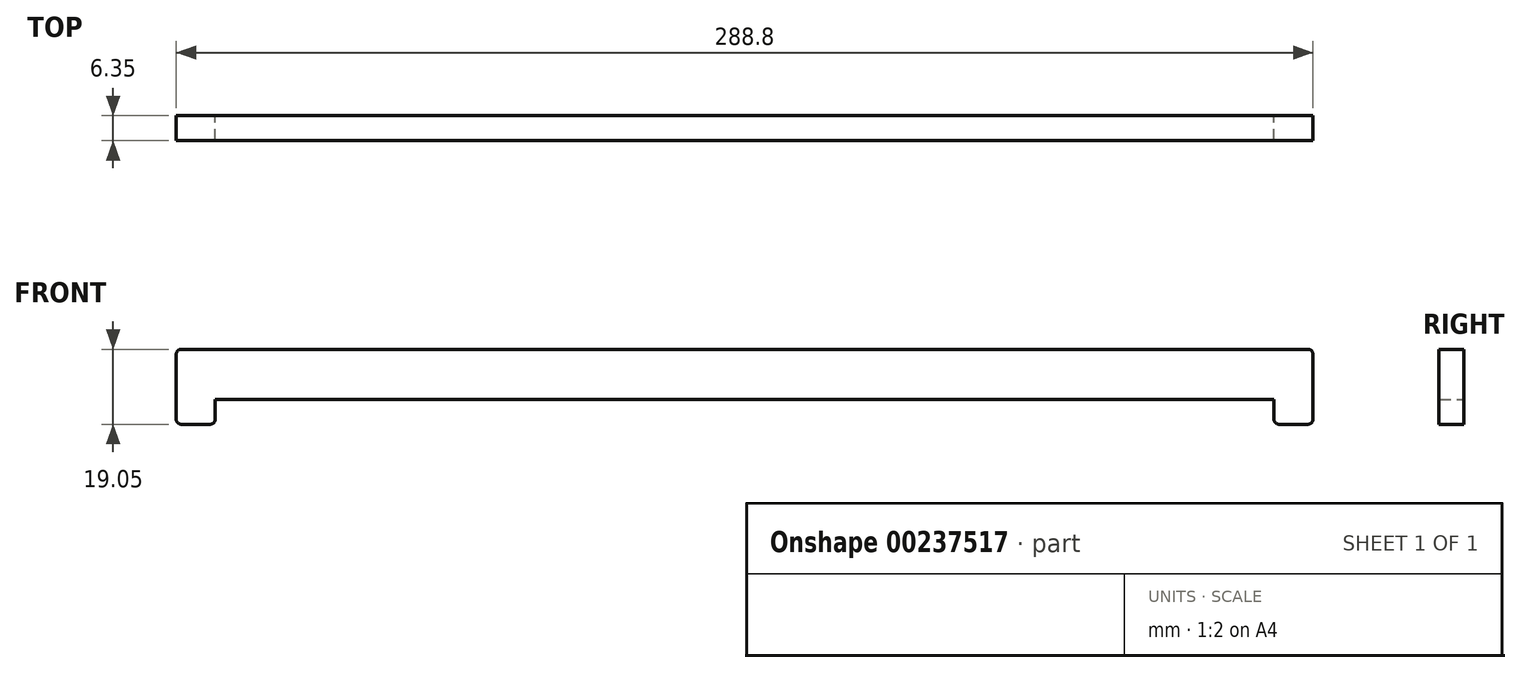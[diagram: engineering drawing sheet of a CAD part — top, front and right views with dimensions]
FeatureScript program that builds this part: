
annotation { "Feature Type Name" : "Feature", "Feature Type Description" : "" }
export const myFeature = defineFeature(function(context is Context, id is Id, definition is map)
    precondition{}
    {
        {
            var Q0;
            Q0=qCreatedBy(makeId("Front.planeOp"),FACE);
            var sketch = newSketch(context, id + "F0", { "sketchPlane" : qUnion([Q0])});
            skLineSegment(sketch, "E0", {"start": v(0, 1.27) * mm, "end": v(0, 17.78) * mm});
            skLineSegment(sketch, "E1", {"start": v(1.27, 19.05) * mm, "end": v(287.53, 19.05) * mm});
            skLineSegment(sketch, "E2", {"start": v(288.8, 17.78) * mm, "end": v(288.8, 1.27) * mm});
            skLineSegment(sketch, "E3", {"start": v(287.53, 0) * mm, "end": v(280.16, 0) * mm});
            skLineSegment(sketch, "E4", {"start": v(278.9, 1.27) * mm, "end": v(278.9, 6.35) * mm});
            skLineSegment(sketch, "E5", {"start": v(278.9, 6.35) * mm, "end": v(9.9, 6.35) * mm});
            skLineSegment(sketch, "E6", {"start": v(9.9, 6.35) * mm, "end": v(9.9, 1.27) * mm});
            skLineSegment(sketch, "E7", {"start": v(8.64, 0) * mm, "end": v(1.27, 0) * mm});
            skPoint(sketch, "E8.visualSharp", {"position": v(0, 19.05) * mm});
            skArc(sketch, "E8.filletArc", {"start": v(1.27, 19.05) * mm, "mid": v(0.37, 18.68) * mm, "end": v(0, 17.78) * mm});
            skPoint(sketch, "E9.visualSharp", {"position": v(0, 0) * mm});
            skArc(sketch, "E9.filletArc", {"start": v(0, 1.27) * mm, "mid": v(0.37, 0.37) * mm, "end": v(1.27, 0) * mm});
            skPoint(sketch, "E10.visualSharp", {"position": v(9.9, 0) * mm});
            skArc(sketch, "E10.filletArc", {"start": v(8.64, 0) * mm, "mid": v(9.53, 0.37) * mm, "end": v(9.9, 1.27) * mm});
            skPoint(sketch, "E11.visualSharp", {"position": v(278.9, 0) * mm});
            skArc(sketch, "E11.filletArc", {"start": v(278.9, 1.27) * mm, "mid": v(279.26, 0.37) * mm, "end": v(280.16, 0) * mm});
            skPoint(sketch, "E12.visualSharp", {"position": v(288.8, 0) * mm});
            skArc(sketch, "E12.filletArc", {"start": v(287.53, 0) * mm, "mid": v(288.43, 0.37) * mm, "end": v(288.8, 1.27) * mm});
            skPoint(sketch, "E13.visualSharp", {"position": v(288.8, 19.05) * mm});
            skArc(sketch, "E13.filletArc", {"start": v(288.8, 17.78) * mm, "mid": v(288.43, 18.68) * mm, "end": v(287.53, 19.05) * mm});
            skSolve(sketch);
        }
        {
            var Q0;
            Q0=makeQuery(id+"F0.imprint","IMPRINT",FACE,{"disambiguationData":[TD([[makeQuery(id+"F0.imprint","IMPRINT",EDGE,{"derivedFrom":sQuery(id+"F0.wireOp",EDGE,"E0")}),-1.0]])]});
            extrude(context, id + "F1", {"entities" : qUnion([Q0]), "depth" : 6.35 * mm, "offsetDistance" : 25.4 * mm});
        }
    });
